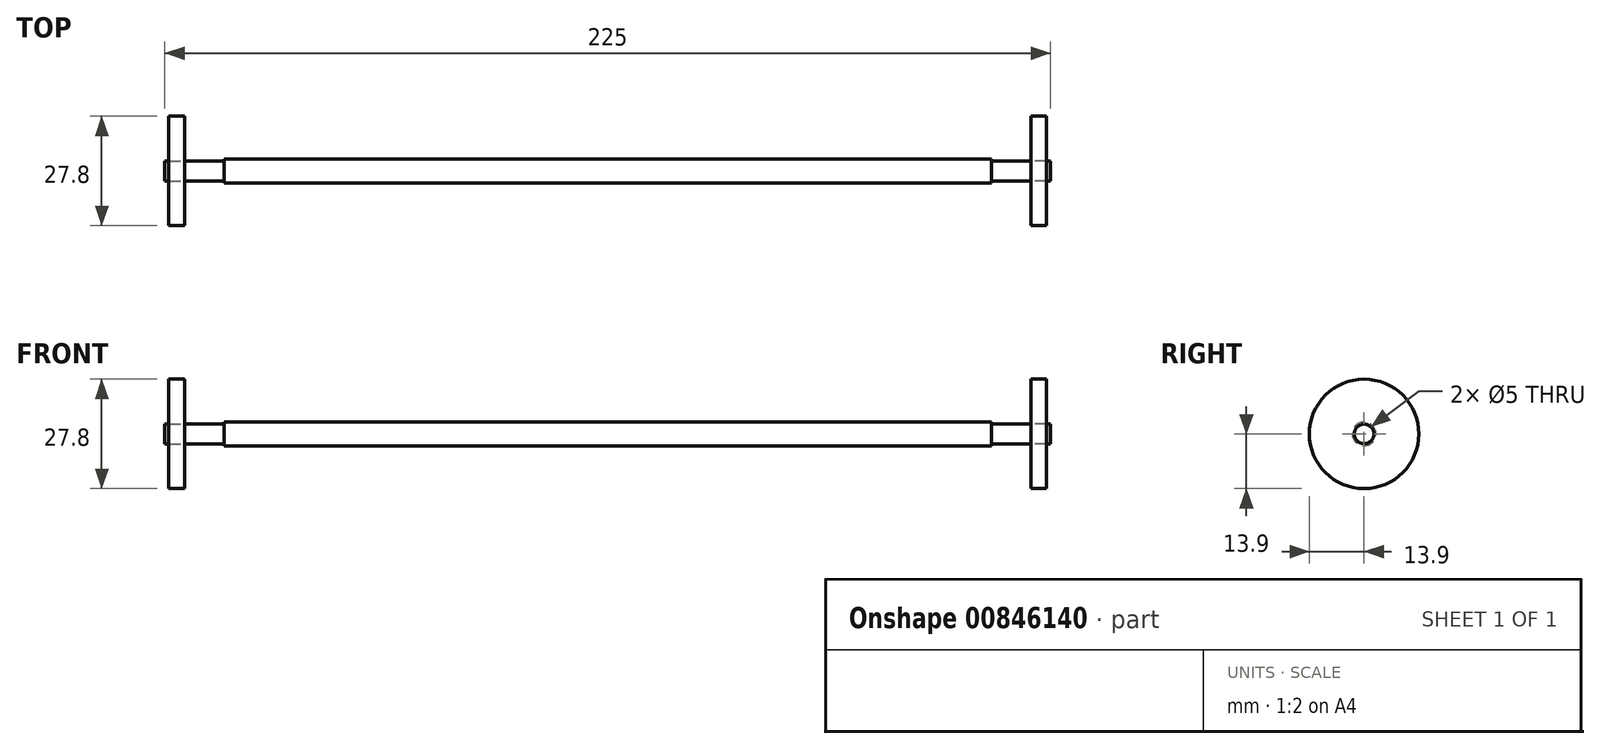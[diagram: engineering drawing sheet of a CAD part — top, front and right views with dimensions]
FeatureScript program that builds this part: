
annotation { "Feature Type Name" : "Feature", "Feature Type Description" : "" }
export const myFeature = defineFeature(function(context is Context, id is Id, definition is map)
    precondition{}
    {
        {
            var Q0;
            Q0=qCreatedBy(makeId("Right.planeOp"),FACE);
            var sketch = newSketch(context, id + "F0", { "sketchPlane" : qUnion([Q0])});
            skCircle(sketch, "E0", {"center": v(0, 0) * mm, "radius": 3 * mm});
            skSolve(sketch);
        }
        {
            var Q0;
            Q0=makeQuery(id+"F0.imprint","IMPRINT",FACE,{"disambiguationData":[TD([[makeQuery(id+"F0.imprint","IMPRINT",EDGE,{"derivedFrom":sQuery(id+"F0.wireOp",EDGE,"E0")}),1.0]])]});
            extrude(context, id + "F1", {"entities" : qUnion([Q0]), "depth" : 195 * mm, "offsetDistance" : 25 * mm});
        }
        {
            var Q0;
            Q0=makeQuery(id+"F1.opExtrude","CAP_FACE",FACE,{"disambiguationData":[OSD([sQuery(id+"F0.wireOp",EDGE,"E0")])],"isStart":true});
            var sketch = newSketch(context, id + "F2", { "sketchPlane" : qUnion([Q0])});
            skCircle(sketch, "E1", {"center": v(0, 0) * mm, "radius": 2.5 * mm});
            skSolve(sketch);
        }
        {
            var Q0;
            Q0=makeQuery(id+"F2.imprint","IMPRINT",FACE,{"disambiguationData":[TD([[makeQuery(id+"F2.imprint","IMPRINT",EDGE,{"derivedFrom":sQuery(id+"F2.wireOp",EDGE,"E1")}),1.0]])]});
            var Q1;
            Q1=makeQuery(id+"F1.opExtrude","CAP_FACE",FACE,{"disambiguationData":[OSD([sQuery(id+"F0.wireOp",EDGE,"E0")])],"isStart":false});
            extrude(context, id + "F3", {"entities" : qUnion([Q0, Q1]), "operationType" : NewBodyOperationType.ADD, "depth" : 10 * mm, "offsetDistance" : 25 * mm});
        }
        {
            var Q0;
            Q0=makeQuery(id+"F1.opExtrude","CAP_FACE",FACE,{"disambiguationData":[OSD([sQuery(id+"F0.wireOp",EDGE,"E0")])],"isStart":false});
            var sketch = newSketch(context, id + "F4", { "sketchPlane" : qUnion([Q0])});
            skCircle(sketch, "E2", {"center": v(0, 0) * mm, "radius": 2.5 * mm});
            skSolve(sketch);
        }
        {
            var Q0;
            Q0=makeQuery(id+"F4.imprint","IMPRINT",FACE,{"disambiguationData":[TD([[makeQuery(id+"F4.imprint","IMPRINT",EDGE,{"derivedFrom":sQuery(id+"F4.wireOp",EDGE,"E2")}),1.0]])]});
            extrude(context, id + "F5", {"entities" : qUnion([Q0]), "operationType" : NewBodyOperationType.ADD, "depth" : 10 * mm, "offsetDistance" : 25 * mm});
        }
        {
            var Q0;
            Q0=makeQuery(id+"F3.opExtrude","CAP_FACE",FACE,{"disambiguationData":[OSD([sQuery(id+"F2.wireOp",EDGE,"E1")])],"isStart":false});
            var sketch = newSketch(context, id + "F6", { "sketchPlane" : qUnion([Q0])});
            skCircle(sketch, "E3", {"center": v(0, 0) * mm, "radius": 13.9 * mm});
            skSolve(sketch);
        }
        {
            var Q0;
            Q0=makeQuery(id+"F6.imprint","IMPRINT",FACE,{"disambiguationData":[TD([[makeQuery(id+"F6.imprint","IMPRINT",EDGE,{"derivedFrom":sQuery(id+"F6.wireOp",EDGE,"E3")}),1.0]])]});
            extrude(context, id + "F7", {"entities" : qUnion([Q0]), "depth" : 4 * mm, "offsetDistance" : 25 * mm});
        }
        {
            var Q0;
            Q0=makeQuery(id+"F3.opExtrude","CAP_FACE",FACE,{"disambiguationData":[OSD([sQuery(id+"F2.wireOp",EDGE,"E1")])],"isStart":false});
            var sketch = newSketch(context, id + "F8", { "sketchPlane" : qUnion([Q0])});
            skSolve(sketch);
        }
        {
            var Q0;
            Q0=makeQuery(id+"F8.imprint","IMPRINT",FACE,{"disambiguationData":[TD([[makeQuery(id+"F8.imprint","IMPRINT",EDGE,{"derivedFrom":makeQuery(id+"F3.opExtrude","CAP_EDGE",EDGE,{"disambiguationData":[OSD([sQuery(id+"F2.wireOp",EDGE,"E1")])],"isStart":false})}),1.0]])]});
            extrude(context, id + "F9", {"entities" : qUnion([Q0]), "depth" : 5 * mm, "offsetDistance" : 25 * mm});
        }
        {
            var Q0;
            Q0=makeQuery(id+"F5.opExtrude","CAP_FACE",FACE,{"disambiguationData":[OSD([sQuery(id+"F4.wireOp",EDGE,"E2")])],"isStart":false});
            var sketch = newSketch(context, id + "F10", { "sketchPlane" : qUnion([Q0])});
            skCircle(sketch, "E4", {"center": v(0, 0) * mm, "radius": 13.9 * mm});
            skSolve(sketch);
        }
        {
            var Q0;
            Q0=makeQuery(id+"F10.imprint","IMPRINT",FACE,{"disambiguationData":[TD([[makeQuery(id+"F10.imprint","IMPRINT",EDGE,{"derivedFrom":sQuery(id+"F10.wireOp",EDGE,"E4")}),1.0]])]});
            extrude(context, id + "F11", {"entities" : qUnion([Q0]), "depth" : 4 * mm, "offsetDistance" : 25 * mm});
        }
        {
            var Q0;
            Q0=makeQuery(id+"F5.opExtrude","CAP_FACE",FACE,{"disambiguationData":[OSD([sQuery(id+"F4.wireOp",EDGE,"E2")])],"isStart":false});
            var sketch = newSketch(context, id + "F12", { "sketchPlane" : qUnion([Q0])});
            skSolve(sketch);
        }
        {
            var Q0;
            Q0=makeQuery(id+"F12.imprint","IMPRINT",FACE,{"disambiguationData":[TD([[makeQuery(id+"F12.imprint","IMPRINT",EDGE,{"derivedFrom":makeQuery(id+"F5.opExtrude","CAP_EDGE",EDGE,{"disambiguationData":[OSD([sQuery(id+"F4.wireOp",EDGE,"E2")])],"isStart":false})}),1.0]])]});
            extrude(context, id + "F13", {"entities" : qUnion([Q0]), "depth" : 5 * mm, "offsetDistance" : 25 * mm});
        }
    });
